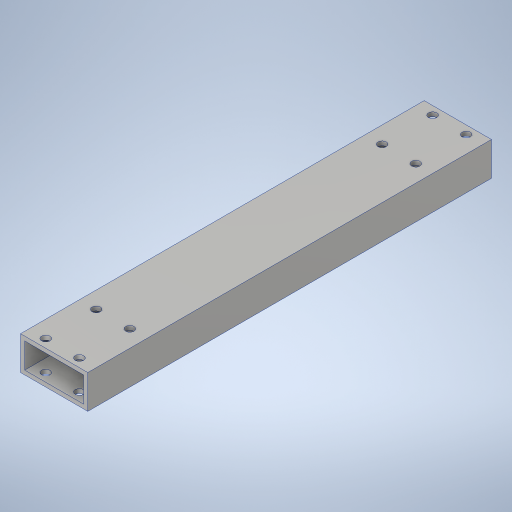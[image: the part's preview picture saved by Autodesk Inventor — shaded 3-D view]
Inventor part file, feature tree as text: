
AUTODESK INVENTOR PART (.ipt)
format: ipt  version: 2023.4 (Build 274418000, 418)  size: 257,536 bytes
history: native  units: in
note: dims shown in document units (in); Inventor stores cm internally (conversion verified against a paired STEP export)
features: sketch x2, extrude x1, hole x1
ambient origin geometry x8: Origin, YZ Plane, XZ Plane, XY Plane, X Axis, Y Axis, Z Axis, Center Point
bodies: Solid1 (feature_tree)
feature tree (4):
  extrude  "Extrusion1"  Depth=1.0in
  hole  "Hole1"  [1 undecoded]
  sketch  "Sketch1"  dims[d0=2.0in d1=1.0in]
  sketch  "Sketch2"  dims[d2=0.125in d3=0.125in d4=12.0in d5=0.0in d6=0.25in d7=1.0in d8=1.5in d9=0.25in d10=0.5in d11=0.5in d12=0.5in d13=1.5in d14=0.25in d15=0.75in d16=0.375in d17=0.25in d18=0.5635in d19=1.0in d20=0.8108in]
note: 1 required parameter value undecoded (feature->parameter linkage not recoverable at this tier; creation-order binding heuristic only, values carry confidence <= 0.55)
